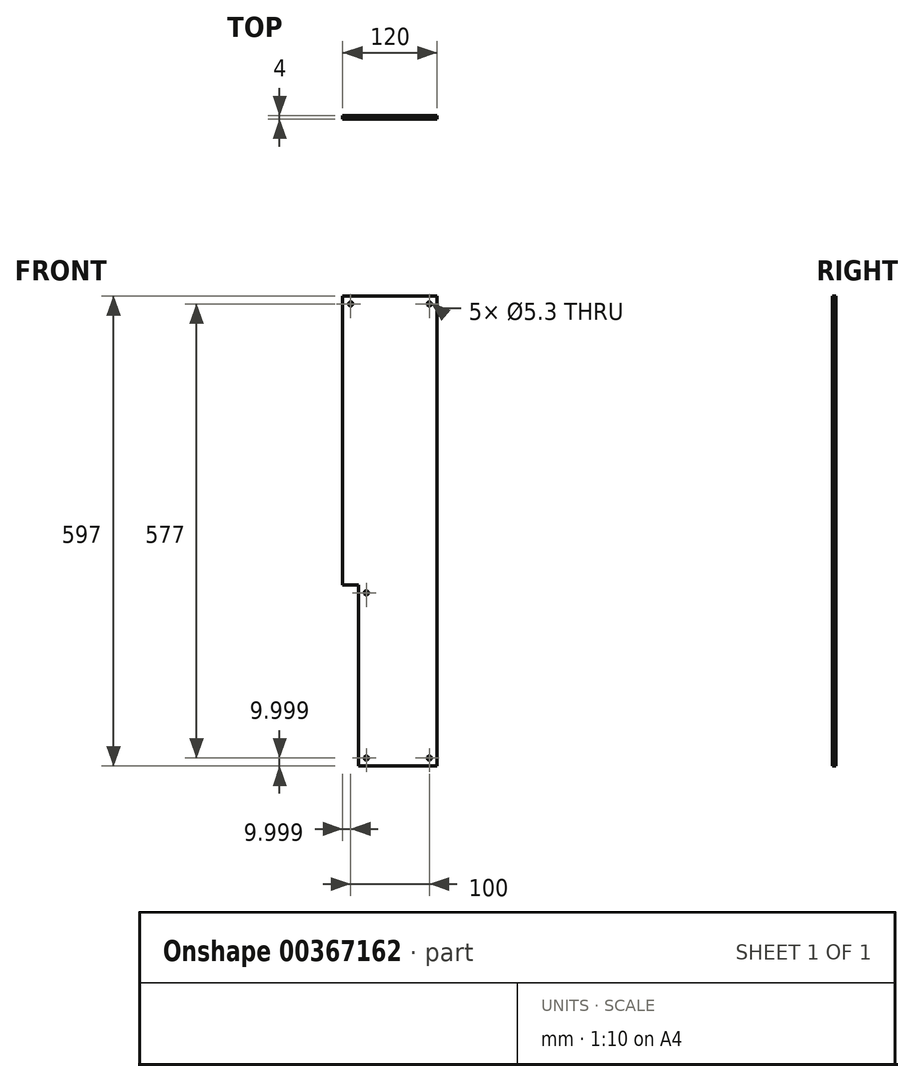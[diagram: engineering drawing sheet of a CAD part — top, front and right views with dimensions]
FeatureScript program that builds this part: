
annotation { "Feature Type Name" : "Feature", "Feature Type Description" : "" }
export const myFeature = defineFeature(function(context is Context, id is Id, definition is map)
    precondition{}
    {
        {
            var Q0;
            Q0=qCreatedBy(makeId("Front.planeOp"),FACE);
            var sketch = newSketch(context, id + "F0", { "sketchPlane" : qUnion([Q0])});
            skLineSegment(sketch, "E0.bottom", {"start": v(-144.86, -11.76) * mm, "end": v(-204.86, -11.76) * mm});
            skLineSegment(sketch, "E0.top", {"start": v(-144.86, 355.24) * mm, "end": v(-204.86, 355.24) * mm});
            skLineSegment(sketch, "E0.left", {"start": v(-144.86, -11.76) * mm, "end": v(-144.86, 355.24) * mm, "construction": true});
            skLineSegment(sketch, "E0.right", {"start": v(-204.86, -11.76) * mm, "end": v(-204.86, 355.24) * mm});
            skLineSegment(sketch, "E1.bottom", {"start": v(-144.86, 355.24) * mm, "end": v(-84.86, 355.24) * mm});
            skLineSegment(sketch, "E1.top", {"start": v(-144.86, -11.76) * mm, "end": v(-84.86, -11.76) * mm, "construction": true});
            skLineSegment(sketch, "E1.left", {"start": v(-144.86, 355.24) * mm, "end": v(-144.86, -11.76) * mm, "construction": true});
            skLineSegment(sketch, "E1.right", {"start": v(-84.86, 355.24) * mm, "end": v(-84.86, -11.76) * mm});
            skLineSegment(sketch, "E2.bottom", {"start": v(-84.86, -11.76) * mm, "end": v(-134.86, -11.76) * mm, "construction": true});
            skLineSegment(sketch, "E2.top", {"start": v(-84.86, -241.76) * mm, "end": v(-134.86, -241.76) * mm});
            skLineSegment(sketch, "E2.left", {"start": v(-84.86, -11.76) * mm, "end": v(-84.86, -241.76) * mm});
            skLineSegment(sketch, "E2.right", {"start": v(-134.86, -11.76) * mm, "end": v(-134.86, -241.76) * mm, "construction": true});
            skLineSegment(sketch, "E3.bottom", {"start": v(-134.86, -241.76) * mm, "end": v(-184.86, -241.76) * mm});
            skLineSegment(sketch, "E3.top", {"start": v(-134.86, -11.76) * mm, "end": v(-184.86, -11.76) * mm, "construction": true});
            skLineSegment(sketch, "E3.left", {"start": v(-134.86, -241.76) * mm, "end": v(-134.86, -11.76) * mm, "construction": true});
            skLineSegment(sketch, "E3.right", {"start": v(-184.86, -241.76) * mm, "end": v(-184.86, -11.76) * mm});
            skLineSegment(sketch, "E4.bottom", {"start": v(-194.86, 345.24) * mm, "end": v(-204.86, 345.24) * mm, "construction": true});
            skLineSegment(sketch, "E4.top", {"start": v(-194.86, 355.24) * mm, "end": v(-204.86, 355.24) * mm, "construction": true});
            skLineSegment(sketch, "E4.left", {"start": v(-194.86, 345.24) * mm, "end": v(-194.86, 355.24) * mm, "construction": true});
            skLineSegment(sketch, "E4.right", {"start": v(-204.86, 345.24) * mm, "end": v(-204.86, 355.24) * mm, "construction": true});
            skCircle(sketch, "E5", {"center": v(-194.86, 345.24) * mm, "radius": 2.65 * mm});
            skCircle(sketch, "E6.MirrorC", {"center": v(-94.86, 345.24) * mm, "radius": 2.65 * mm});
            skLineSegment(sketch, "E7.bottom", {"start": v(-184.86, -241.76) * mm, "end": v(-174.86, -241.76) * mm, "construction": true});
            skLineSegment(sketch, "E7.top", {"start": v(-184.86, -231.76) * mm, "end": v(-174.86, -231.76) * mm, "construction": true});
            skLineSegment(sketch, "E7.left", {"start": v(-184.86, -241.76) * mm, "end": v(-184.86, -231.76) * mm, "construction": true});
            skLineSegment(sketch, "E7.right", {"start": v(-174.86, -241.76) * mm, "end": v(-174.86, -231.76) * mm, "construction": true});
            skCircle(sketch, "E8", {"center": v(-174.86, -231.76) * mm, "radius": 2.65 * mm});
            skCircle(sketch, "E9.MirrorC", {"center": v(-94.86, -231.76) * mm, "radius": 2.65 * mm});
            skLineSegment(sketch, "E10.bottom", {"start": v(-184.86, -11.76) * mm, "end": v(-174.86, -11.76) * mm, "construction": true});
            skLineSegment(sketch, "E10.top", {"start": v(-184.86, -21.76) * mm, "end": v(-174.86, -21.76) * mm, "construction": true});
            skLineSegment(sketch, "E10.left", {"start": v(-184.86, -11.76) * mm, "end": v(-184.86, -21.76) * mm, "construction": true});
            skLineSegment(sketch, "E10.right", {"start": v(-174.86, -11.76) * mm, "end": v(-174.86, -21.76) * mm, "construction": true});
            skCircle(sketch, "E11", {"center": v(-174.86, -21.76) * mm, "radius": 2.65 * mm});
            skSolve(sketch);
        }
        {
            var Q0;
            Q0=makeQuery(id+"F0.imprint","IMPRINT",FACE,{"disambiguationData":[TD([[makeQuery(id+"F0.imprint","IMPRINT",EDGE,{"derivedFrom":sQuery(id+"F0.wireOp",EDGE,"E0.top")}),1.0]])]});
            extrude(context, id + "F1", {"entities" : qUnion([Q0]), "depth" : 4 * mm});
        }
    });
